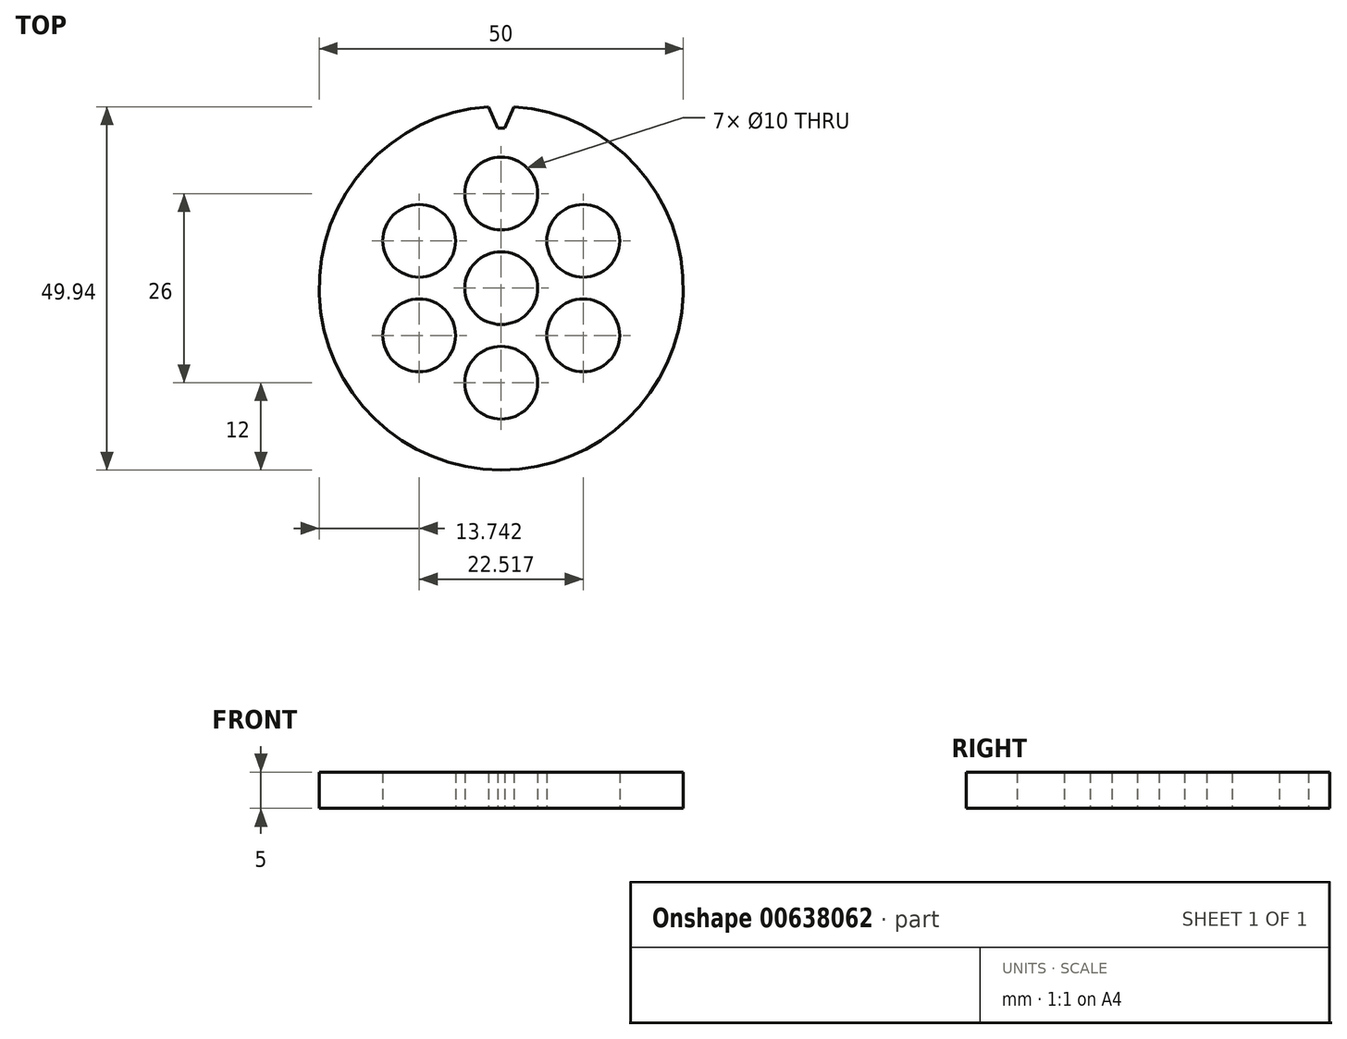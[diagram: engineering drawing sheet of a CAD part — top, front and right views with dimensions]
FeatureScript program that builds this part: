
annotation { "Feature Type Name" : "Feature", "Feature Type Description" : "" }
export const myFeature = defineFeature(function(context is Context, id is Id, definition is map)
    precondition{}
    {
        {
            var Q0;
            Q0=qCreatedBy(makeId("Top.planeOp"),FACE);
            var sketch = newSketch(context, id + "F0", { "sketchPlane" : qUnion([Q0])});
            skCircle(sketch, "E0", {"center": v(0, 0) * mm, "radius": 25 * mm});
            skCircle(sketch, "E1", {"center": v(0, 0) * mm, "radius": 5 * mm});
            skLineSegment(sketch, "E2", {"start": v(1.72, 24.94) * mm, "end": v(0.5, 22) * mm});
            skLineSegment(sketch, "E3.MirrorCS", {"start": v(-1.72, 24.94) * mm, "end": v(-0.5, 22) * mm});
            skCircle(sketch, "E4", {"center": v(0, 0) * mm, "radius": 22 * mm});
            skCircle(sketch, "E5", {"center": v(0, 13) * mm, "radius": 5 * mm});
            skSolve(sketch);
        }
        {
            var Q0;
            Q0=makeQuery(id+"F0.imprint","IMPRINT",FACE,{"disambiguationData":[TD([[makeQuery(id+"F0.imprint","IMPRINT",EDGE,{"derivedFrom":sQuery(id+"F0.wireOp",EDGE,"E1")}),-1.0]])]});
            var Q1;
            {var subQ0=sQuery(id+"F0.wireOp",EDGE,"E2");Q1=makeQuery(id+"F0.imprint","IMPRINT",FACE,{"disambiguationData":[TD([[makeQuery(id+"F0.imprint","IMPRINT",EDGE,{"derivedFrom":subQ0}),1.0]])]});}
            var Q2;
            {var subQ0=sQuery(id+"F0.wireOp",EDGE,"E2");Q2=makeQuery(id+"F0.imprint","IMPRINT",FACE,{"disambiguationData":[TD([[makeQuery(id+"F0.imprint","IMPRINT",EDGE,{"derivedFrom":subQ0}),-1.0]])]});}
            extrude(context, id + "F1", {"entities" : qUnion([Q0, Q1, Q2]), "depth" : 5 * mm, "offsetDistance" : 25 * mm});
        }
        {
            var Q0;
            {var subQ0=sQuery(id+"F0.wireOp",EDGE,"E2");Q0=makeQuery(id+"F0.imprint","IMPRINT",FACE,{"disambiguationData":[TD([[makeQuery(id+"F0.imprint","IMPRINT",EDGE,{"derivedFrom":subQ0}),-1.0]])]});}
            extrude(context, id + "F2", {"entities" : qUnion([Q0]), "operationType" : NewBodyOperationType.REMOVE, "endBound" : BoundingType.THROUGH_ALL, "depth" : 25 * mm, "offsetDistance" : 25 * mm});
        }
        {
            var Q0;
            Q0=makeQuery(id+"F1.opExtrude","SWEPT_FACE",FACE,{"disambiguationData":[OSD([sQuery(id+"F0.wireOp",EDGE,"E5")])]});
            var Q1;
            Q1=makeQuery(id+"F1.opExtrude","SWEPT_FACE",FACE,{"disambiguationData":[OSD([sQuery(id+"F0.wireOp",EDGE,"E1")])]});
            circularPattern(context, id + "F3", {"patternType" : PatternType.FACE, "faces" : qUnion([Q0]), "axis" : qUnion([Q1]), "angle" : 360 * degree, "instanceCount" : 6, "equalSpace" : true});
        }
    });
